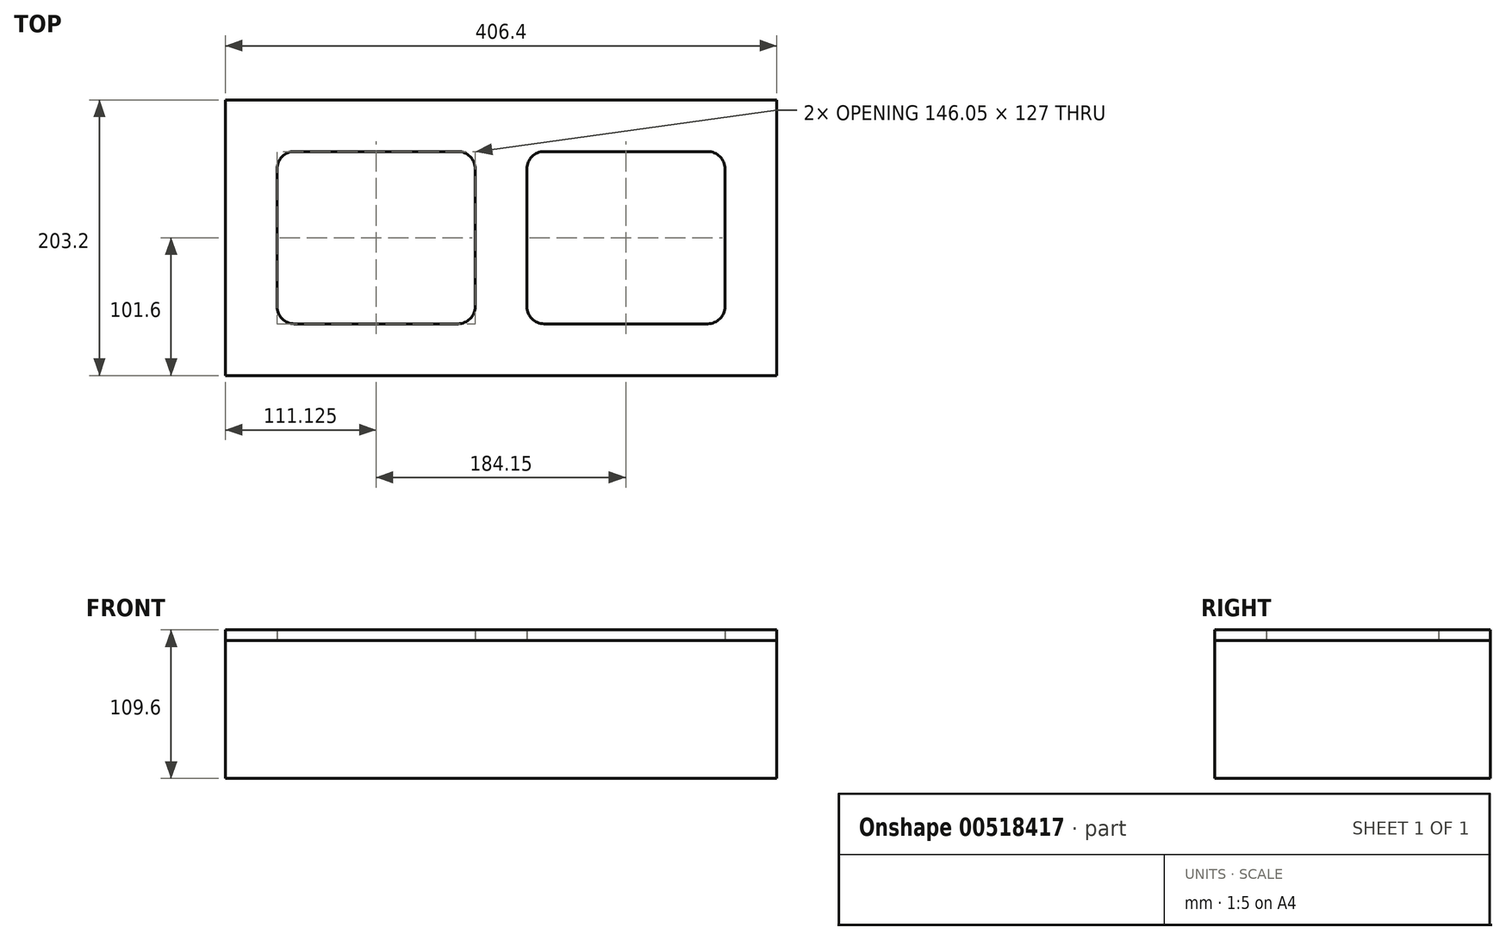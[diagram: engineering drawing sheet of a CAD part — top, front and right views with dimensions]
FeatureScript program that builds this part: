
annotation { "Feature Type Name" : "Feature", "Feature Type Description" : "" }
export const myFeature = defineFeature(function(context is Context, id is Id, definition is map)
    precondition{}
    {
        {
            assignVariable(context, id + "F0", {"name" : "CinderBlockHeight", "anyValue" : 8});
        }
        {
            var Q0;
            Q0=qCreatedBy(makeId("Top.planeOp"),FACE);
            var sketch = newSketch(context, id + "F1", { "sketchPlane" : qUnion([Q0])});
            skLineSegment(sketch, "E0.bottom", {"start": v(203.2, 101.6) * mm, "end": v(-203.2, 101.6) * mm});
            skLineSegment(sketch, "E0.top", {"start": v(203.2, -101.6) * mm, "end": v(-203.2, -101.6) * mm});
            skLineSegment(sketch, "E0.left", {"start": v(203.2, 101.6) * mm, "end": v(203.2, -101.6) * mm});
            skLineSegment(sketch, "E0.right", {"start": v(-203.2, 101.6) * mm, "end": v(-203.2, -101.6) * mm});
            skPoint(sketch, "E0.middle", {"position": v(0, 0) * mm});
            skLineSegment(sketch, "E1.bottom", {"start": v(-152.4, 63.5) * mm, "end": v(-31.75, 63.5) * mm});
            skLineSegment(sketch, "E1.top", {"start": v(-152.4, -63.5) * mm, "end": v(-31.75, -63.5) * mm});
            skLineSegment(sketch, "E1.left", {"start": v(-165.1, 50.8) * mm, "end": v(-165.1, -50.8) * mm});
            skLineSegment(sketch, "E1.right", {"start": v(-19.05, 50.8) * mm, "end": v(-19.05, -50.8) * mm});
            skLineSegment(sketch, "E2.MirrorCS", {"start": v(19.05, 50.8) * mm, "end": v(19.05, -50.8) * mm});
            skLineSegment(sketch, "E3.MirrorCS", {"start": v(165.1, 50.8) * mm, "end": v(165.1, -50.8) * mm});
            skLineSegment(sketch, "E4.MirrorCS", {"start": v(152.4, -63.5) * mm, "end": v(31.75, -63.5) * mm});
            skLineSegment(sketch, "E5.MirrorCS", {"start": v(152.4, 63.5) * mm, "end": v(31.75, 63.5) * mm});
            skPoint(sketch, "E6.visualSharp", {"position": v(165.1, -63.5) * mm});
            skArc(sketch, "E6.filletArc", {"start": v(152.4, -63.5) * mm, "mid": v(161.38, -59.78) * mm, "end": v(165.1, -50.8) * mm});
            skPoint(sketch, "E7.visualSharp", {"position": v(19.05, -63.5) * mm});
            skArc(sketch, "E7.filletArc", {"start": v(19.05, -50.8) * mm, "mid": v(22.77, -59.78) * mm, "end": v(31.75, -63.5) * mm});
            skPoint(sketch, "E8.visualSharp", {"position": v(19.05, 63.5) * mm});
            skArc(sketch, "E8.filletArc", {"start": v(31.75, 63.5) * mm, "mid": v(22.77, 59.78) * mm, "end": v(19.05, 50.8) * mm});
            skPoint(sketch, "E9.visualSharp", {"position": v(165.1, 63.5) * mm});
            skArc(sketch, "E9.filletArc", {"start": v(165.1, 50.8) * mm, "mid": v(161.38, 59.78) * mm, "end": v(152.4, 63.5) * mm});
            skPoint(sketch, "E10.visualSharp", {"position": v(-19.05, -63.5) * mm});
            skArc(sketch, "E10.filletArc", {"start": v(-31.75, -63.5) * mm, "mid": v(-22.77, -59.78) * mm, "end": v(-19.05, -50.8) * mm});
            skPoint(sketch, "E11.visualSharp", {"position": v(-165.1, -63.5) * mm});
            skArc(sketch, "E11.filletArc", {"start": v(-165.1, -50.8) * mm, "mid": v(-161.38, -59.78) * mm, "end": v(-152.4, -63.5) * mm});
            skPoint(sketch, "E12.visualSharp", {"position": v(-165.1, 63.5) * mm});
            skArc(sketch, "E12.filletArc", {"start": v(-152.4, 63.5) * mm, "mid": v(-161.38, 59.78) * mm, "end": v(-165.1, 50.8) * mm});
            skPoint(sketch, "E13.visualSharp", {"position": v(-19.05, 63.5) * mm});
            skArc(sketch, "E13.filletArc", {"start": v(-19.05, 50.8) * mm, "mid": v(-22.77, 59.78) * mm, "end": v(-31.75, 63.5) * mm});
            skSolve(sketch);
        }
        {
            var Q0;
            Q0=makeQuery(id+"F1.imprint","IMPRINT",FACE,{"disambiguationData":[TD([[makeQuery(id+"F1.imprint","IMPRINT",EDGE,{"derivedFrom":sQuery(id+"F1.wireOp",EDGE,"E0.bottom")}),1.0]])]});
            extrude(context, id + "F2", {"entities" : qUnion([Q0]), "depth" : (getVariable(context, 'CinderBlockHeight')) * mm, "offsetDistance" : 25.4 * mm});
        }
        {
            var Q0;
            Q0=makeQuery(id+"F1.imprint","IMPRINT",FACE,{"disambiguationData":[TD([[makeQuery(id+"F1.imprint","IMPRINT",EDGE,{"derivedFrom":sQuery(id+"F1.wireOp",EDGE,"E0.bottom")}),1.0]])]});
            var Q1;
            Q1=makeQuery(id+"F1.imprint","IMPRINT",FACE,{"disambiguationData":[TD([[makeQuery(id+"F1.imprint","IMPRINT",EDGE,{"derivedFrom":sQuery(id+"F1.wireOp",EDGE,"E1.bottom")}),-1.0]])]});
            var Q2;
            Q2=makeQuery(id+"F1.imprint","IMPRINT",FACE,{"disambiguationData":[TD([[makeQuery(id+"F1.imprint","IMPRINT",EDGE,{"derivedFrom":sQuery(id+"F1.wireOp",EDGE,"E2.MirrorCS")}),1.0]])]});
            extrude(context, id + "F3", {"entities" : qUnion([Q0, Q1, Q2]), "oppositeDirection" : true, "depth" : 101.6 * mm, "offsetDistance" : 25.4 * mm});
        }
    });
